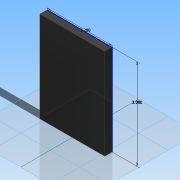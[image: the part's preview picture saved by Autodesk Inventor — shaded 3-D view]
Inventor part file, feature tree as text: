
AUTODESK INVENTOR PART (.ipt)
format: ipt  version: 2014 SP2 (Build 180246200, 246)  size: 76,288 bytes
history: native  units: in
note: dims shown in document units (in); Inventor stores cm internally (conversion verified against a paired STEP export)
features: sketch x1, extrude x1
ambient origin geometry x8: Origin, YZ Plane, XZ Plane, XY Plane, X Axis, Y Axis, Z Axis, Center Point
bodies: Solid1 (feature_tree)
feature tree (2):
  sketch  "Sketch1"  dims[d0=0.25in d1=0.0in d2=2.2in d3=3.08in]
  extrude  "Extrusion1"  Depth=2.2in
